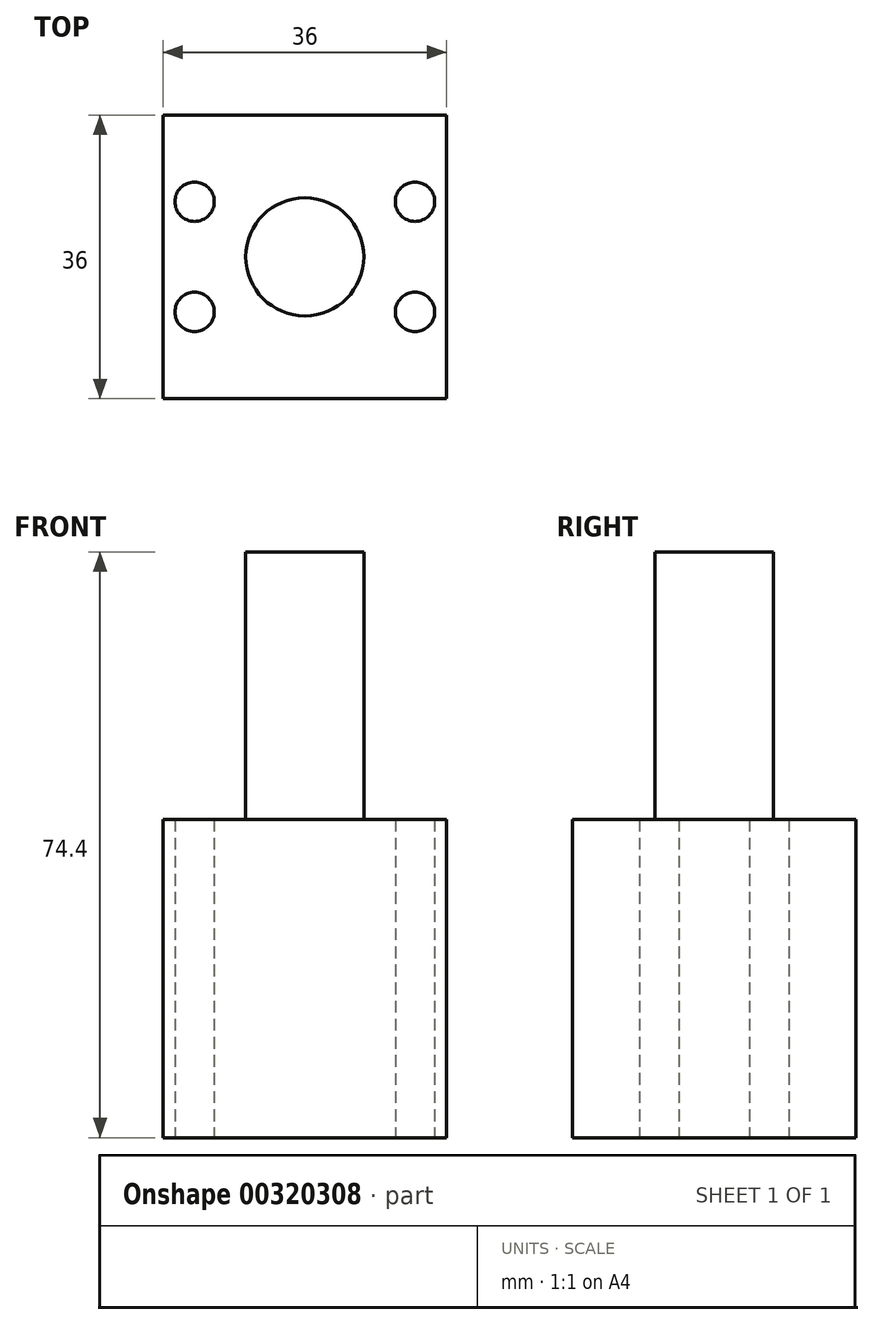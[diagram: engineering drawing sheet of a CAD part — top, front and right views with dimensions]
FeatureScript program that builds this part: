
annotation { "Feature Type Name" : "Feature", "Feature Type Description" : "" }
export const myFeature = defineFeature(function(context is Context, id is Id, definition is map)
    precondition{}
    {
        {
            var Q0;
            Q0=qCreatedBy(makeId("Top.planeOp"),FACE);
            var sketch = newSketch(context, id + "F0", { "sketchPlane" : qUnion([Q0])});
            skLineSegment(sketch, "E0.bottom", {"start": v(-18, 18) * mm, "end": v(18, 18) * mm});
            skLineSegment(sketch, "E0.top", {"start": v(-18, -18) * mm, "end": v(18, -18) * mm});
            skLineSegment(sketch, "E0.left", {"start": v(-18, 18) * mm, "end": v(-18, -18) * mm});
            skLineSegment(sketch, "E0.right", {"start": v(18, 18) * mm, "end": v(18, -18) * mm});
            skPoint(sketch, "E0.middle", {"position": v(0, 0) * mm});
            skCircle(sketch, "E1", {"center": v(0, 0) * mm, "radius": 7.5 * mm});
            skSolve(sketch);
        }
        {
            var Q0;
            Q0=makeQuery(id+"F0.imprint","IMPRINT",FACE,{"disambiguationData":[TD([[makeQuery(id+"F0.imprint","IMPRINT",EDGE,{"derivedFrom":sQuery(id+"F0.wireOp",EDGE,"E1")}),1.0]])]});
            extrude(context, id + "F1", {"entities" : qUnion([Q0]), "depth" : 74.4 * mm});
        }
        {
            var Q0;
            Q0 = qSketchRegion(id + "F0", true);
            extrude(context, id + "F2", {"entities" : qUnion([Q0]), "operationType" : NewBodyOperationType.ADD, "depth" : 40.4 * mm});
        }
        {
            var Q0;
            Q0=qCreatedBy(makeId("Top.planeOp"),FACE);
            var sketch = newSketch(context, id + "F3", { "sketchPlane" : qUnion([Q0])});
            skPoint(sketch, "E2", {"position": v(-14, 7) * mm});
            skPoint(sketch, "E3", {"position": v(-14, -7) * mm});
            skPoint(sketch, "E4", {"position": v(14, -7) * mm});
            skPoint(sketch, "E5", {"position": v(14, 7) * mm});
            skSolve(sketch);
        }
        {
            var Q0;
            Q0=sQuery(id+"F3.wireOp",VERTEX,"E2");
            var Q1;
            Q1=sQuery(id+"F3.wireOp",VERTEX,"E5");
            var Q2;
            Q2=sQuery(id+"F3.wireOp",VERTEX,"E4");
            var Q3;
            Q3=sQuery(id+"F3.wireOp",VERTEX,"E3");
            var Q4;
            Q4=makeQuery(id+"F1.opExtrude","SWEPT_BODY",BODY,{"disambiguationData":[OSD([sQuery(id+"F0.wireOp",EDGE,"E1")])]});
            hole(context, id + "F4", {"style" : HoleStyle.SIMPLE, "endStyle" : HoleEndStyle.THROUGH, "oppositeDirection" : true, "holeDiameter" : 5 * mm, "tappedDepth" : 12 * mm, "tapClearance" : 3, "locations" : qUnion([Q0, Q1, Q2, Q3]), "scope" : qUnion([Q4])});
        }
    });
